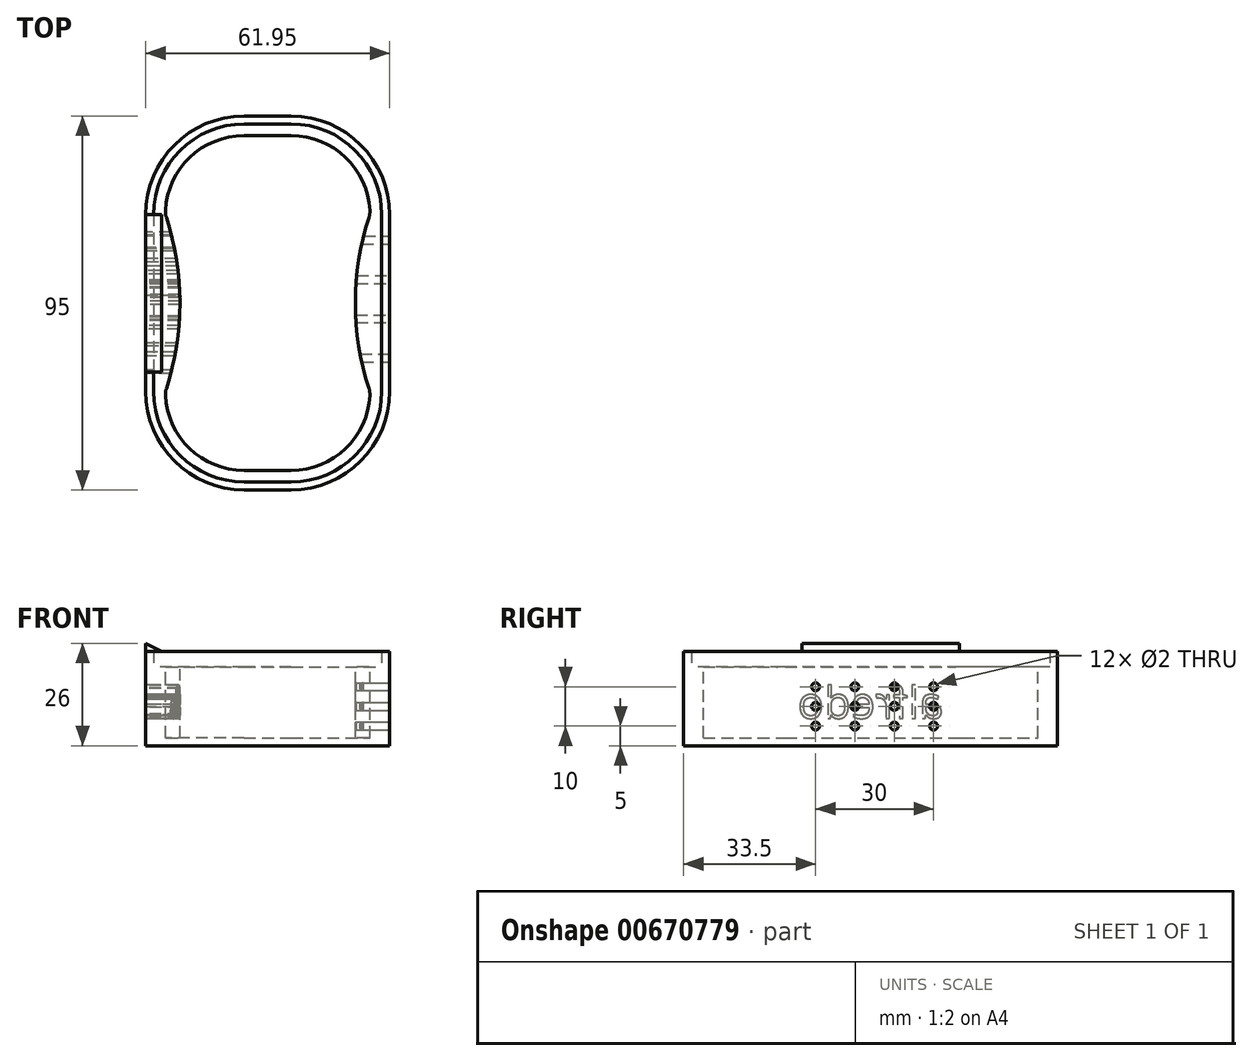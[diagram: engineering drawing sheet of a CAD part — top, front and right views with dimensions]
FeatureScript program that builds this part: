
annotation { "Feature Type Name" : "Feature", "Feature Type Description" : "" }
export const myFeature = defineFeature(function(context is Context, id is Id, definition is map)
    precondition{}
    {
        {
            var Q0;
            Q0=qCreatedBy(makeId("Top.planeOp"),FACE);
            cPlane(context, id + "F0", {"entities" : qUnion([Q0]), "cplaneType" : CPlaneType.OFFSET, "offset" : 20 * mm, "oppositeDirection" : true, "width" : 150 * mm, "height" : 150 * mm});
        }
        {
            var Q0;
            Q0=qCreatedBy(id+"F0.planeOp",FACE);
            var sketch = newSketch(context, id + "F1", { "sketchPlane" : qUnion([Q0])});
            skLineSegment(sketch, "E0.bottom", {"start": v(-4.97, 90) * mm, "end": v(56.97, 90) * mm});
            skLineSegment(sketch, "E0.top", {"start": v(-4.97, -5) * mm, "end": v(56.97, -5) * mm});
            skLineSegment(sketch, "E0.left", {"start": v(-4.97, 90) * mm, "end": v(-4.97, -5) * mm});
            skLineSegment(sketch, "E0.right", {"start": v(56.97, 90) * mm, "end": v(56.97, -5) * mm});
            skSolve(sketch);
        }
        {
            var Q0;
            Q0=qCreatedBy(makeId("Top.planeOp"),FACE);
            var sketch = newSketch(context, id + "F2", { "sketchPlane" : qUnion([Q0])});
            skLineSegment(sketch, "E1", {"start": v(0, 100) * mm, "end": v(0, -100) * mm, "construction": true});
            skLineSegment(sketch, "E2", {"start": v(-100, 0) * mm, "end": v(100, 0) * mm, "construction": true});
            skLineSegment(sketch, "E3.bottom", {"start": v(20, 0) * mm, "end": v(32, 0) * mm});
            skLineSegment(sketch, "E3.top", {"start": v(20, 85) * mm, "end": v(32, 85) * mm});
            skPoint(sketch, "E4.visualSharp", {"position": v(0, 85) * mm});
            skArc(sketch, "E4.filletArc", {"start": v(20, 85) * mm, "mid": v(6.22, 79.5) * mm, "end": v(0.03, 66) * mm});
            skPoint(sketch, "E5.visualSharp", {"position": v(52, 85) * mm});
            skArc(sketch, "E5.filletArc", {"start": v(51.97, 66) * mm, "mid": v(45.78, 79.5) * mm, "end": v(32, 85) * mm});
            skPoint(sketch, "E6.visualSharp", {"position": v(52, 0) * mm});
            skArc(sketch, "E6.filletArc", {"start": v(32, 0) * mm, "mid": v(45.78, 5.5) * mm, "end": v(51.97, 19) * mm});
            skPoint(sketch, "E7.visualSharp", {"position": v(0, 0) * mm});
            skArc(sketch, "E7.filletArc", {"start": v(0.03, 19) * mm, "mid": v(6.22, 5.5) * mm, "end": v(20, 0) * mm});
            skArc(sketch, "E8", {"start": v(0.27, 20.8) * mm, "mid": v(3.71, 42.5) * mm, "end": v(0.27, 64.2) * mm});
            skArc(sketch, "E9", {"start": v(51.73, 64.2) * mm, "mid": v(48.29, 42.5) * mm, "end": v(51.73, 20.8) * mm});
            skPoint(sketch, "E10.visualSharp", {"position": v(52, 65) * mm});
            skArc(sketch, "E10.filletArc", {"start": v(51.73, 64.2) * mm, "mid": v(51.94, 65.1) * mm, "end": v(51.97, 66) * mm});
            skPoint(sketch, "E11.visualSharp", {"position": v(52, 20) * mm});
            skArc(sketch, "E11.filletArc", {"start": v(51.97, 19) * mm, "mid": v(51.94, 19.9) * mm, "end": v(51.73, 20.8) * mm});
            skPoint(sketch, "E12.visualSharp", {"position": v(0, 20) * mm});
            skArc(sketch, "E12.filletArc", {"start": v(0.27, 20.8) * mm, "mid": v(0.06, 19.9) * mm, "end": v(0.03, 19) * mm});
            skPoint(sketch, "E13.visualSharp", {"position": v(0, 65) * mm});
            skArc(sketch, "E13.filletArc", {"start": v(0.03, 66) * mm, "mid": v(0.06, 65.1) * mm, "end": v(0.27, 64.2) * mm});
            skSolve(sketch);
        }
        {
            var Q0;
            Q0 = qSketchRegion(id + "F1", true);
            extrude(context, id + "F3", {"entities" : qUnion([Q0]), "depth" : 20 * mm, "offsetDistance" : 25 * mm});
        }
        {
            var Q0;
            Q0 = qSketchRegion(id + "F2", true);
            extrude(context, id + "F4", {"entities" : qUnion([Q0]), "operationType" : NewBodyOperationType.REMOVE, "oppositeDirection" : true, "depth" : 18 * mm, "offsetDistance" : 25 * mm});
        }
        {
            var Q0;
            Q0=makeQuery(id+"F3.opExtrude","SWEPT_EDGE",EDGE,{"disambiguationData":[OSD([sQuery(id+"F1.wireOp",EDGE,"E0.top"),sQuery(id+"F1.wireOp",EDGE,"E0.left")])]});
            var Q1;
            Q1=makeQuery(id+"F3.opExtrude","SWEPT_EDGE",EDGE,{"disambiguationData":[OSD([sQuery(id+"F1.wireOp",EDGE,"E0.top"),sQuery(id+"F1.wireOp",EDGE,"E0.right")])]});
            var Q2;
            Q2=makeQuery(id+"F3.opExtrude","SWEPT_EDGE",EDGE,{"disambiguationData":[OSD([sQuery(id+"F1.wireOp",EDGE,"E0.bottom"),sQuery(id+"F1.wireOp",EDGE,"E0.left")])]});
            var Q3;
            Q3=makeQuery(id+"F3.opExtrude","SWEPT_EDGE",EDGE,{"disambiguationData":[OSD([sQuery(id+"F1.wireOp",EDGE,"E0.bottom"),sQuery(id+"F1.wireOp",EDGE,"E0.right")])]});
            fillet(context, id + "F5", {"entities" : qUnion([Q0, Q1, Q2, Q3]), "radius" : 25 * mm, "tangentPropagation" : true, "allowEdgeOverflow" : false});
        }
        {
            var Q0;
            Q0=makeQuery(id+"F3.opExtrude","SWEPT_FACE",FACE,{"disambiguationData":[OSD([sQuery(id+"F1.wireOp",EDGE,"E0.left")])]});
            var sketch = newSketch(context, id + "F6", { "sketchPlane" : qUnion([Q0])});
            skText(sketch, "E14", { "text": "alfredo", "fontName": "OpenSans-Regular.ttf"});
            const initialGuessF6  = {"E14": [-0.06097, -0.01302, 1, 0, 0.008]};
            skSetInitialGuess(sketch, initialGuessF6);
            skSolve(sketch);
        }
        {
            var Q0;
            Q0 = qSketchRegion(id + "F6", true);
            extrude(context, id + "F7", {"entities" : qUnion([Q0]), "operationType" : NewBodyOperationType.REMOVE, "endBound" : BoundingType.UP_TO_NEXT, "oppositeDirection" : true, "depth" : 25 * mm, "offsetDistance" : 25 * mm});
        }
        {
            var Q0;
            Q0=makeQuery(id+"F3.opExtrude","SWEPT_FACE",FACE,{"disambiguationData":[OSD([sQuery(id+"F1.wireOp",EDGE,"E0.right")])]});
            var sketch = newSketch(context, id + "F8", { "sketchPlane" : qUnion([Q0])});
            skCircle(sketch, "E15", {"center": v(28.5, -15) * mm, "radius": 1 * mm});
            skCircle(sketch, "E16.0.1.0", {"center": v(28.5, -10) * mm, "radius": 1 * mm});
            skCircle(sketch, "E16.0.2.0", {"center": v(28.5, -5) * mm, "radius": 1 * mm});
            skCircle(sketch, "E16.1.0.0", {"center": v(38.5, -15) * mm, "radius": 1 * mm});
            skCircle(sketch, "E16.1.1.0", {"center": v(38.5, -10) * mm, "radius": 1 * mm});
            skCircle(sketch, "E16.1.2.0", {"center": v(38.5, -5) * mm, "radius": 1 * mm});
            skCircle(sketch, "E16.2.0.0", {"center": v(48.5, -15) * mm, "radius": 1 * mm});
            skCircle(sketch, "E16.2.1.0", {"center": v(48.5, -10) * mm, "radius": 1 * mm});
            skCircle(sketch, "E16.2.2.0", {"center": v(48.5, -5) * mm, "radius": 1 * mm});
            skCircle(sketch, "E16.3.0.0", {"center": v(58.5, -15) * mm, "radius": 1 * mm});
            skCircle(sketch, "E16.3.1.0", {"center": v(58.5, -10) * mm, "radius": 1 * mm});
            skCircle(sketch, "E16.3.2.0", {"center": v(58.5, -5) * mm, "radius": 1 * mm});
            skLineSegment(sketch, "E16.direction1", {"start": v(28.5, -15) * mm, "end": v(38.5, -15) * mm, "construction": true});
            skLineSegment(sketch, "E16.direction2", {"start": v(28.5, -15) * mm, "end": v(28.5, -10) * mm, "construction": true});
            skSolve(sketch);
        }
        {
            var Q0;
            Q0 = qSketchRegion(id + "F8", true);
            extrude(context, id + "F9", {"entities" : qUnion([Q0]), "operationType" : NewBodyOperationType.REMOVE, "endBound" : BoundingType.UP_TO_NEXT, "oppositeDirection" : true, "depth" : 25 * mm, "offsetDistance" : 25 * mm});
        }
        {
            var Q0;
            Q0=makeQuery(id+"F3.opExtrude","CAP_FACE",FACE,{"disambiguationData":[OSD([sQuery(id+"F1.wireOp",EDGE,"E0.bottom"),sQuery(id+"F1.wireOp",EDGE,"E0.top"),sQuery(id+"F1.wireOp",EDGE,"E0.left"),sQuery(id+"F1.wireOp",EDGE,"E0.right")])],"isStart":false});
            var sketch = newSketch(context, id + "F10", { "sketchPlane" : qUnion([Q0])});
            skArc(sketch, "E17.0", {"start": v(20.03, 88) * mm, "mid": v(3.76, 81.26) * mm, "end": v(-2.97, 65) * mm});
            skLineSegment(sketch, "E17.1", {"start": v(31.97, 88) * mm, "end": v(20.03, 88) * mm});
            skLineSegment(sketch, "E17.2", {"start": v(-2.97, 65) * mm, "end": v(-2.97, 20) * mm});
            skArc(sketch, "E17.3", {"start": v(54.97, 65) * mm, "mid": v(48.24, 81.26) * mm, "end": v(31.97, 88) * mm});
            skArc(sketch, "E17.4", {"start": v(-2.97, 20) * mm, "mid": v(3.76, 3.74) * mm, "end": v(20.03, -3) * mm});
            skLineSegment(sketch, "E17.5", {"start": v(20.03, -3) * mm, "end": v(31.97, -3) * mm});
            skArc(sketch, "E17.6", {"start": v(31.97, -3) * mm, "mid": v(48.24, 3.74) * mm, "end": v(54.97, 20) * mm});
            skLineSegment(sketch, "E17.7", {"start": v(54.97, 20) * mm, "end": v(54.97, 65) * mm});
            skSolve(sketch);
        }
        {
            var Q0;
            Q0=makeQuery(id+"F10.imprint","IMPRINT",FACE,{"disambiguationData":[TD([[makeQuery(id+"F10.imprint","IMPRINT",EDGE,{"derivedFrom":sQuery(id+"F10.wireOp",EDGE,"E17.0")}),-1.0]])]});
            extrude(context, id + "F11", {"entities" : qUnion([Q0]), "operationType" : NewBodyOperationType.ADD, "depth" : 4 * mm, "offsetDistance" : 25 * mm});
        }
        {
            var Q0;
            Q0=qCreatedBy(makeId("Front.planeOp"),FACE);
            cPlane(context, id + "F12", {"entities" : qUnion([Q0]), "cplaneType" : CPlaneType.OFFSET, "offset" : 45 * mm, "oppositeDirection" : true, "width" : 150 * mm, "height" : 150 * mm});
        }
        {
            var Q0;
            Q0=qCreatedBy(id+"F12.planeOp",FACE);
            var sketch = newSketch(context, id + "F13", { "sketchPlane" : qUnion([Q0])});
            skLineSegment(sketch, "E18", {"start": v(-8.23, 4) * mm, "end": v(3.7, 4) * mm, "construction": true});
            skLineSegment(sketch, "E19", {"start": v(-4.98, 2.96) * mm, "end": v(-4.98, 5.5) * mm, "construction": true});
            skLineSegment(sketch, "E20", {"start": v(-4.98, 4) * mm, "end": v(-4.98, 6) * mm});
            skPoint(sketch, "E20.startSnap0", {"position": v(-4.98, 4.23) * mm});
            skLineSegment(sketch, "E21", {"start": v(-4.98, 6) * mm, "end": v(-0.98, 4) * mm});
            skLineSegment(sketch, "E22", {"start": v(-0.98, 4) * mm, "end": v(-4.98, 4) * mm});
            skSolve(sketch);
        }
        {
            var Q0;
            Q0 = qSketchRegion(id + "F13", true);
            extrude(context, id + "F14", {"entities" : qUnion([Q0]), "operationType" : NewBodyOperationType.ADD, "endBound" : BoundingType.SYMMETRIC, "depth" : 40 * mm, "offsetDistance" : 25 * mm});
        }
        {
            var Q0;
            Q0=makeQuery(id+"F11.opExtrude","CAP_EDGE",EDGE,{"disambiguationData":[OSD([sQuery(id+"F1.wireOp",EDGE,"E0.right")])],"isStart":false});
            cPlane(context, id + "F15", {"entities" : qUnion([Q0]), "cplaneType" : CPlaneType.LINE_ANGLE, "offset" : 25 * mm, "angle" : 45 * degree, "oppositeDirection" : true, "width" : 150 * mm, "height" : 150 * mm});
        }
        {
            var Q0;
            Q0=qCreatedBy(id+"F15.planeOp",FACE);
            var sketch = newSketch(context, id + "F16", { "sketchPlane" : qUnion([Q0])});
            skCircle(sketch, "E23", {"center": v(37.5, -42.82) * mm, "radius": 4.23 * mm});
            skSolve(sketch);
        }
        {
            var Q0;
            Q0 = qSketchRegion(id + "F16", true);
            extrude(context, id + "F17", {"entities" : qUnion([Q0]), "operationType" : NewBodyOperationType.REMOVE, "depth" : 50 * mm, "offsetDistance" : 25 * mm});
        }
    });
